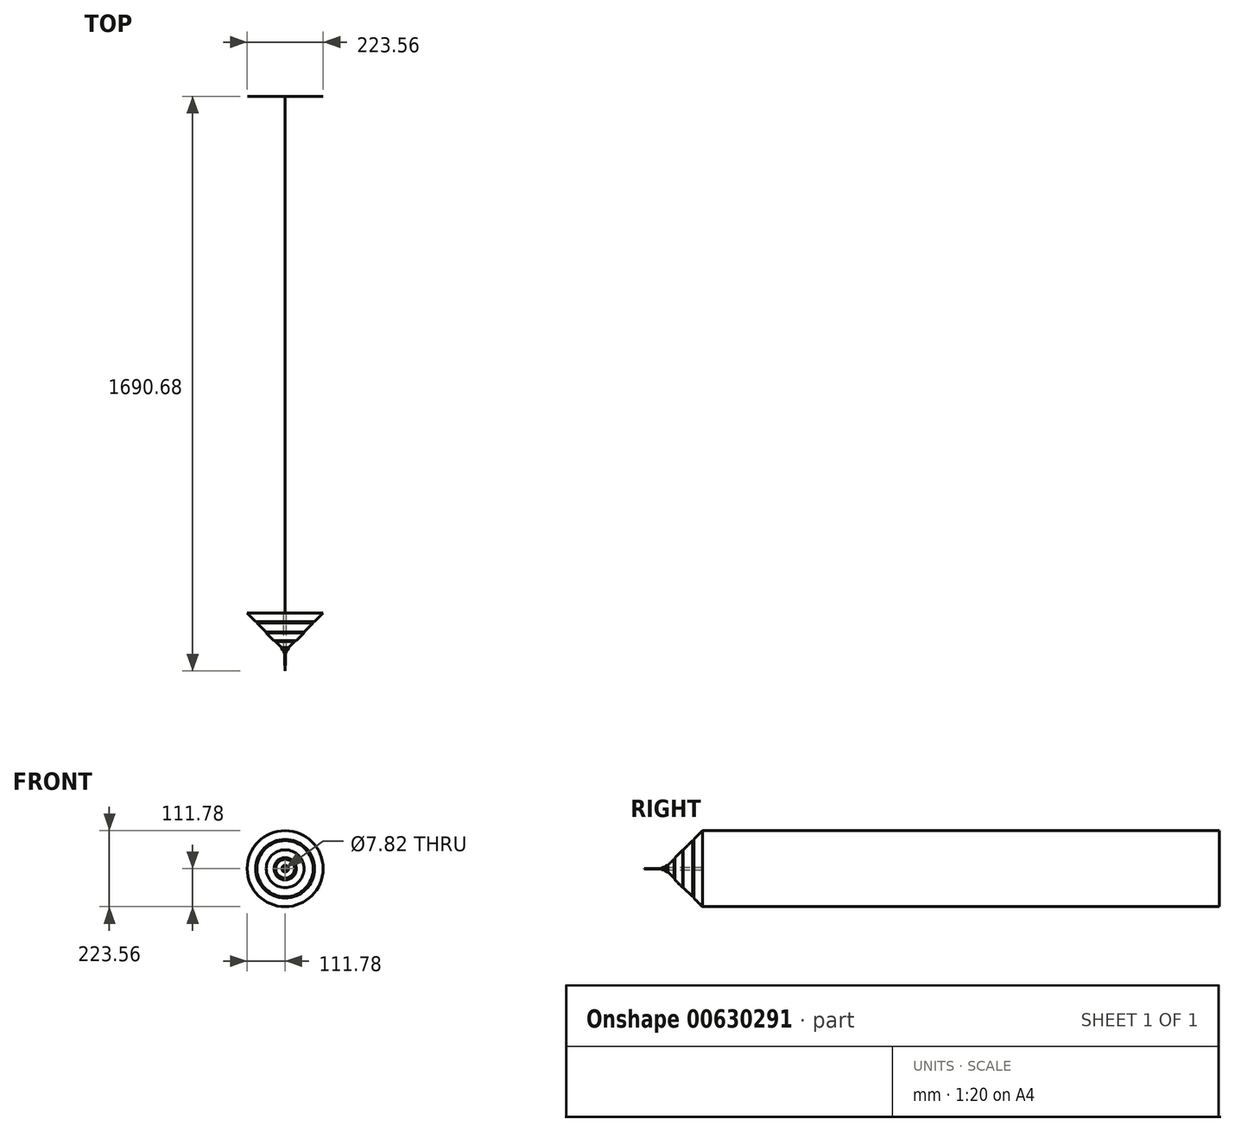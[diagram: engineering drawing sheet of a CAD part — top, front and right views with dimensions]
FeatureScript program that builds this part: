
annotation { "Feature Type Name" : "Feature", "Feature Type Description" : "" }
export const myFeature = defineFeature(function(context is Context, id is Id, definition is map)
    precondition{}
    {
        {
            var Q0;
            Q0=qCreatedBy(makeId("Front.planeOp"),FACE);
            var sketch = newSketch(context, id + "F0", { "sketchPlane" : qUnion([Q0])});
            skCircle(sketch, "E0", {"center": v(0, 0) * mm, "radius": 116.86 * mm});
            skCircle(sketch, "E1", {"center": v(0, 0) * mm, "radius": 82.69 * mm});
            skCircle(sketch, "E2", {"center": v(0, 0) * mm, "radius": 55.56 * mm});
            skCircle(sketch, "E3", {"center": v(0, 0) * mm, "radius": 27.63 * mm});
            skCircle(sketch, "E4", {"center": v(0, 0) * mm, "radius": 9.86 * mm});
            skCircle(sketch, "E5", {"center": v(0, 0) * mm, "radius": 3.91 * mm});
            skSolve(sketch);
        }
        {
            var Q0;
            Q0 = qSketchRegion(id + "F0", true);
            extrude(context, id + "F1", {"entities" : qUnion([Q0]), "depth" : 25.4 * mm, "offsetDistance" : 25.4 * mm});
        }
        {
            var Q0;
            Q0=makeQuery(id+"F1.opExtrude","CAP_EDGE",EDGE,{"disambiguationData":[OSD([sQuery(id+"F0.wireOp",EDGE,"E0")])],"isStart":false});
            chamfer(context, id + "F2", {"entities" : qUnion([Q0]), "width" : 30.48 * mm, "tangentPropagation" : true});
        }
        {
            var Q0;
            Q0=makeQuery(id+"F0.imprint","IMPRINT",FACE,{"disambiguationData":[TD([[makeQuery(id+"F0.imprint","IMPRINT",EDGE,{"derivedFrom":sQuery(id+"F0.wireOp",EDGE,"E1")}),1.0]])]});
            extrude(context, id + "F3", {"entities" : qUnion([Q0]), "operationType" : NewBodyOperationType.ADD, "depth" : 57.15 * mm, "offsetDistance" : 25.4 * mm});
        }
        {
            var Q0;
            Q0=makeQuery(id+"F3.opExtrude","CAP_EDGE",EDGE,{"disambiguationData":[OSD([sQuery(id+"F0.wireOp",EDGE,"E1")])],"isStart":false});
            chamfer(context, id + "F4", {"entities" : qUnion([Q0]), "width" : 27.94 * mm, "tangentPropagation" : true});
        }
        {
            var Q0;
            Q0=makeQuery(id+"F0.imprint","IMPRINT",FACE,{"disambiguationData":[TD([[makeQuery(id+"F0.imprint","IMPRINT",EDGE,{"derivedFrom":sQuery(id+"F0.wireOp",EDGE,"E2")}),1.0]])]});
            extrude(context, id + "F5", {"entities" : qUnion([Q0]), "operationType" : NewBodyOperationType.ADD, "depth" : 81.03 * mm, "offsetDistance" : 25.4 * mm});
        }
        {
            var Q0;
            Q0=makeQuery(id+"F5.opExtrude","CAP_EDGE",EDGE,{"disambiguationData":[OSD([sQuery(id+"F0.wireOp",EDGE,"E2")])],"isStart":false});
            chamfer(context, id + "F6", {"entities" : qUnion([Q0]), "width" : 22.86 * mm, "tangentPropagation" : true});
        }
        {
            var Q0;
            Q0=makeQuery(id+"F0.imprint","IMPRINT",FACE,{"disambiguationData":[TD([[makeQuery(id+"F0.imprint","IMPRINT",EDGE,{"derivedFrom":sQuery(id+"F0.wireOp",EDGE,"E3")}),1.0]])]});
            extrude(context, id + "F7", {"entities" : qUnion([Q0]), "operationType" : NewBodyOperationType.ADD, "depth" : 109.22 * mm, "offsetDistance" : 25.4 * mm});
        }
        {
            var Q0;
            Q0=makeQuery(id+"F7.opExtrude","CAP_EDGE",EDGE,{"disambiguationData":[OSD([sQuery(id+"F0.wireOp",EDGE,"E3")])],"isStart":false});
            chamfer(context, id + "F8", {"entities" : qUnion([Q0]), "width" : 25.4 * mm, "tangentPropagation" : true});
        }
        {
            var Q0;
            Q0=makeQuery(id+"F0.imprint","IMPRINT",FACE,{"disambiguationData":[TD([[makeQuery(id+"F0.imprint","IMPRINT",EDGE,{"derivedFrom":sQuery(id+"F0.wireOp",EDGE,"E4")}),1.0]])]});
            extrude(context, id + "F9", {"entities" : qUnion([Q0]), "operationType" : NewBodyOperationType.ADD, "depth" : 113.8 * mm, "offsetDistance" : 25.4 * mm});
        }
        {
            var Q0;
            Q0=makeQuery(id+"F9.opExtrude","CAP_EDGE",EDGE,{"disambiguationData":[OSD([sQuery(id+"F0.wireOp",EDGE,"E4")])],"isStart":false});
            chamfer(context, id + "F10", {"entities" : qUnion([Q0]), "width" : 7.62 * mm, "tangentPropagation" : true});
        }
        {
            var Q0;
            Q0=makeQuery(id+"F0.imprint","IMPRINT",FACE,{"disambiguationData":[TD([[makeQuery(id+"F0.imprint","IMPRINT",EDGE,{"derivedFrom":sQuery(id+"F0.wireOp",EDGE,"E5")}),1.0]])]});
            var sketch = newSketch(context, id + "F11", { "sketchPlane" : qUnion([Q0])});
            skCircle(sketch, "E6", {"center": v(0, 0) * mm, "radius": 3.87 * mm});
            skSolve(sketch);
        }
        {
            var Q0;
            Q0 = qSketchRegion(id + "F11", true);
            extrude(context, id + "F12", {"entities" : qUnion([Q0]), "depth" : 119.89 * mm, "offsetDistance" : 25.4 * mm});
        }
        {
            var Q0;
            Q0=makeQuery(id+"F12.opExtrude","CAP_EDGE",EDGE,{"disambiguationData":[OSD([sQuery(id+"F11.wireOp",EDGE,"E6")])],"isStart":false});
            chamfer(context, id + "F13", {"entities" : qUnion([Q0]), "width" : 2.54 * mm, "tangentPropagation" : true});
        }
        {
            var Q0;
            Q0=qCreatedBy(makeId("Top.planeOp"),FACE);
            var sketch = newSketch(context, id + "F14", { "sketchPlane" : qUnion([Q0])});
            skLineSegment(sketch, "E7.bottom", {"start": v(-111.12, 0) * mm, "end": v(111.42, 0) * mm});
            skLineSegment(sketch, "E7.top", {"start": v(-111.12, 1520.03) * mm, "end": v(111.42, 1520.03) * mm});
            skLineSegment(sketch, "E7.left", {"start": v(-111.12, 0) * mm, "end": v(-111.12, 1520.03) * mm});
            skLineSegment(sketch, "E7.right", {"start": v(111.42, 0) * mm, "end": v(111.42, 1520.03) * mm});
            skSolve(sketch);
        }
        {
            var Q0;
            Q0 = qSketchRegion(id + "F14", true);
            extrude(context, id + "F15", {"entities" : qUnion([Q0]), "endBound" : BoundingType.SYMMETRIC, "depth" : 223.52 * mm, "offsetDistance" : 25.4 * mm});
        }
        {
            var Q0;
            Q0=makeQuery(id+"F15.opExtrude","CAP_EDGE",EDGE,{"disambiguationData":[OSD([sQuery(id+"F14.wireOp",EDGE,"E7.left")])],"isStart":true});
            var Q1;
            Q1=makeQuery(id+"F15.opExtrude","CAP_EDGE",EDGE,{"disambiguationData":[OSD([sQuery(id+"F14.wireOp",EDGE,"E7.right")])],"isStart":true});
            var Q2;
            Q2=makeQuery(id+"F15.opExtrude","CAP_EDGE",EDGE,{"disambiguationData":[OSD([sQuery(id+"F14.wireOp",EDGE,"E7.right")])],"isStart":false});
            var Q3;
            Q3=makeQuery(id+"F15.opExtrude","CAP_EDGE",EDGE,{"disambiguationData":[OSD([sQuery(id+"F14.wireOp",EDGE,"E7.left")])],"isStart":false});
            fillet(context, id + "F16", {"entities" : qUnion([Q0, Q1, Q2, Q3]), "radius" : 112.22 * mm, "tangentPropagation" : true, "allowEdgeOverflow" : false});
        }
        {
            var Q0;
            Q0=qCreatedBy(makeId("Top.planeOp"),FACE);
            var sketch = newSketch(context, id + "F17", { "sketchPlane" : qUnion([Q0])});
            skLineSegment(sketch, "E8.bottom", {"start": v(-1.53, -119.96) * mm, "end": v(1.52, -119.96) * mm});
            skLineSegment(sketch, "E8.top", {"start": v(-1.53, -138.2) * mm, "end": v(1.52, -138.2) * mm});
            skLineSegment(sketch, "E8.left", {"start": v(-1.53, -119.96) * mm, "end": v(-1.53, -138.2) * mm});
            skLineSegment(sketch, "E8.right", {"start": v(1.52, -119.96) * mm, "end": v(1.52, -138.2) * mm});
            skLineSegment(sketch, "E9", {"start": v(-1.53, -138.2) * mm, "end": v(0, -170.65) * mm});
            skLineSegment(sketch, "E10", {"start": v(0, -170.65) * mm, "end": v(1.52, -138.2) * mm});
            skSolve(sketch);
        }
        {
            var Q0;
            Q0 = qSketchRegion(id + "F17", true);
            extrude(context, id + "F18", {"entities" : qUnion([Q0]), "endBound" : BoundingType.SYMMETRIC, "depth" : 1.8 * mm, "offsetDistance" : 25.4 * mm});
        }
    });
